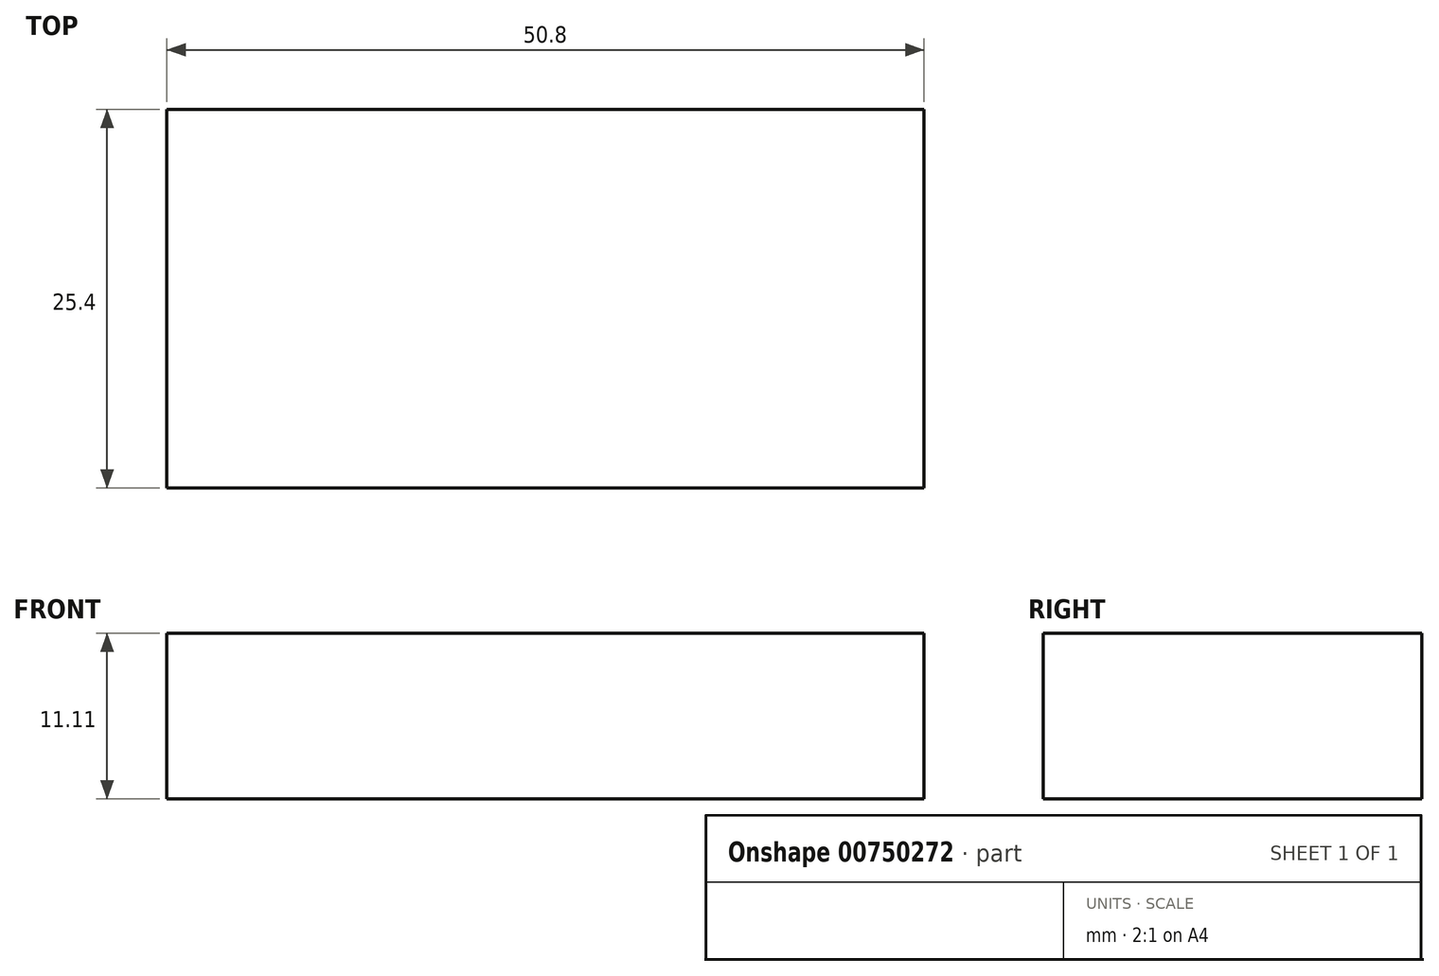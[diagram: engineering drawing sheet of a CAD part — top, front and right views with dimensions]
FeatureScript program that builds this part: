
annotation { "Feature Type Name" : "Feature", "Feature Type Description" : "" }
export const myFeature = defineFeature(function(context is Context, id is Id, definition is map)
    precondition{}
    {
        {
            var Q0;
            Q0=qCreatedBy(makeId("Top.planeOp"),FACE);
            var sketch = newSketch(context, id + "F0", { "sketchPlane" : qUnion([Q0])});
            skLineSegment(sketch, "E0", {"start": v(-34.87, 38.95) * mm, "end": v(15.93, 38.95) * mm});
            skLineSegment(sketch, "E1", {"start": v(15.93, 38.95) * mm, "end": v(15.93, 13.55) * mm});
            skLineSegment(sketch, "E2", {"start": v(15.93, 13.55) * mm, "end": v(-34.87, 13.55) * mm});
            skLineSegment(sketch, "E3", {"start": v(-34.87, 13.55) * mm, "end": v(-34.87, 38.95) * mm});
            skSolve(sketch);
        }
        {
            var Q0;
            Q0=makeQuery(id+"F0.imprint","IMPRINT",FACE,{"disambiguationData":[TD([[makeQuery(id+"F0.imprint","IMPRINT",EDGE,{"derivedFrom":sQuery(id+"F0.wireOp",EDGE,"E0")}),-1.0]])]});
            extrude(context, id + "F1", {"entities" : qUnion([Q0]), "depth" : 11.1 * mm, "offsetDistance" : 25.4 * mm});
        }
    });
